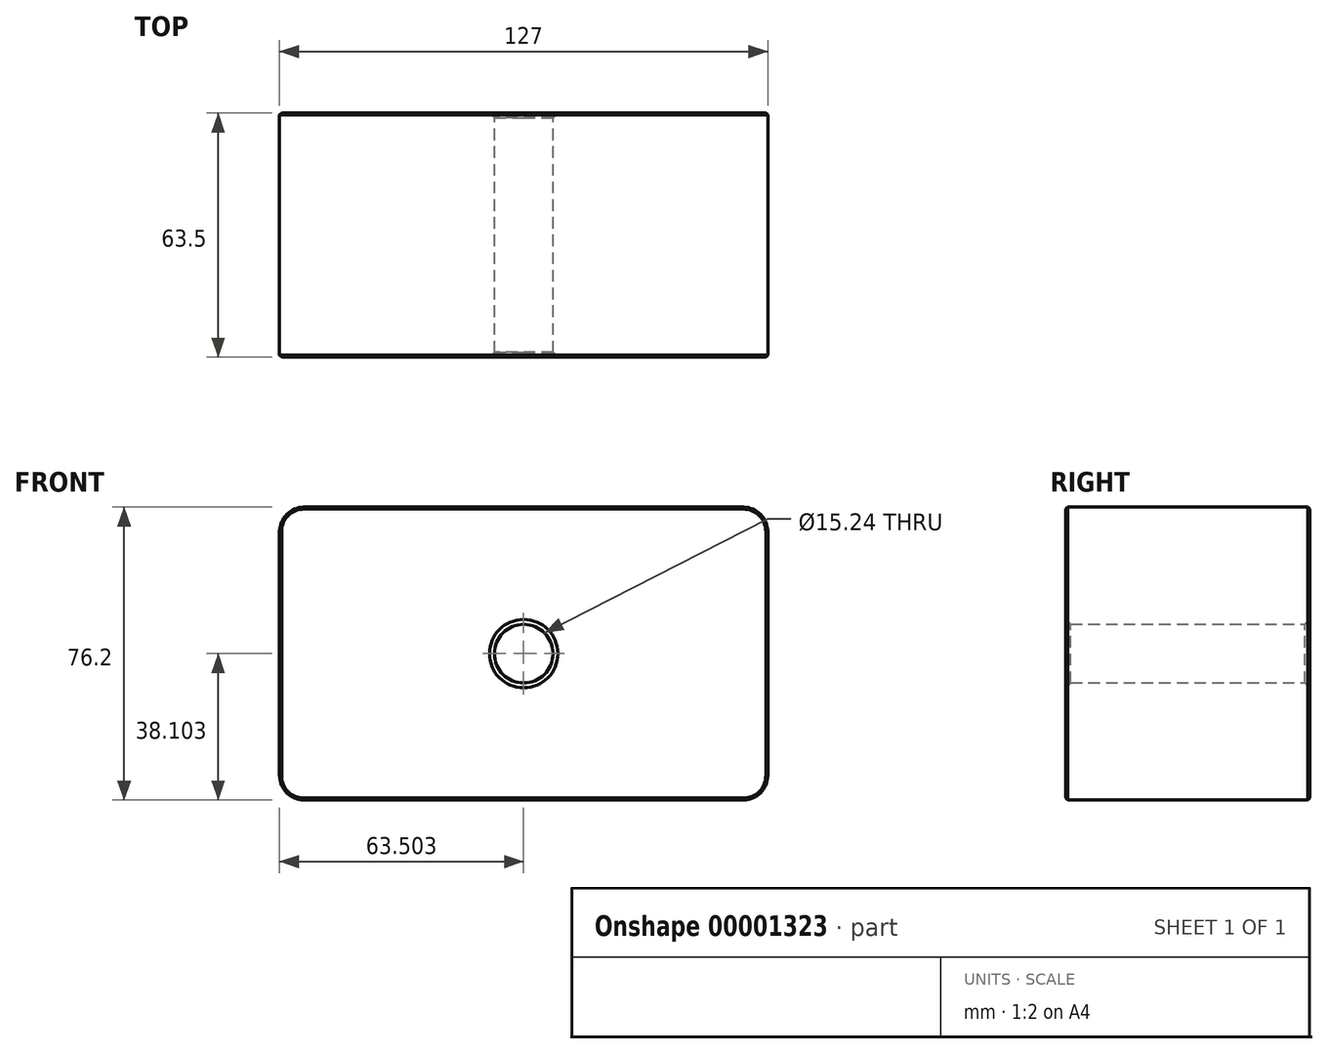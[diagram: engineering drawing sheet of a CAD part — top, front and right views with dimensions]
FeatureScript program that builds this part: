
annotation { "Feature Type Name" : "Feature", "Feature Type Description" : "" }
export const myFeature = defineFeature(function(context is Context, id is Id, definition is map)
    precondition{}
    {
        {
            var Q0;
            Q0=qCreatedBy(makeId("Front.planeOp"),FACE);
            var sketch = newSketch(context, id + "F0", { "sketchPlane" : qUnion([Q0])});
            skLineSegment(sketch, "E0.bottom", {"start": v(-20, 51.34) * mm, "end": v(94.3, 51.34) * mm});
            skLineSegment(sketch, "E0.top", {"start": v(-20, -24.86) * mm, "end": v(94.3, -24.86) * mm});
            skLineSegment(sketch, "E0.left", {"start": v(-26.36, 45) * mm, "end": v(-26.36, -18.5) * mm});
            skLineSegment(sketch, "E0.right", {"start": v(100.64, 45) * mm, "end": v(100.64, -18.5) * mm});
            skCircle(sketch, "E1", {"center": v(37.14, 13.24) * mm, "radius": 7.62 * mm});
            skPoint(sketch, "E2.visualSharp", {"position": v(-26.36, 51.34) * mm});
            skArc(sketch, "E2.filletArc", {"start": v(-20, 51.34) * mm, "mid": v(-24.5, 49.48) * mm, "end": v(-26.36, 45) * mm});
            skPoint(sketch, "E3.visualSharp", {"position": v(100.64, 51.34) * mm});
            skArc(sketch, "E3.filletArc", {"start": v(100.64, 45) * mm, "mid": v(98.78, 49.48) * mm, "end": v(94.3, 51.34) * mm});
            skPoint(sketch, "E4.visualSharp", {"position": v(100.64, -24.86) * mm});
            skArc(sketch, "E4.filletArc", {"start": v(94.3, -24.86) * mm, "mid": v(98.78, -23) * mm, "end": v(100.64, -18.5) * mm});
            skPoint(sketch, "E5.visualSharp", {"position": v(-26.36, -24.86) * mm});
            skArc(sketch, "E5.filletArc", {"start": v(-26.36, -18.5) * mm, "mid": v(-24.5, -23) * mm, "end": v(-20, -24.86) * mm});
            skSolve(sketch);
        }
        {
            var Q0;
            Q0=makeQuery(id+"F0.imprint","IMPRINT",FACE,{"disambiguationData":[TD([[makeQuery(id+"F0.imprint","IMPRINT",EDGE,{"derivedFrom":sQuery(id+"F0.wireOp",EDGE,"E0.bottom")}),-1.0]])]});
            extrude(context, id + "F1", {"entities" : qUnion([Q0]), "depth" : 63.5 * mm});
        }
        {
            var Q0;
            Q0=makeQuery(id+"F1.opExtrude","CAP_EDGE",EDGE,{"disambiguationData":[OSD([sQuery(id+"F0.wireOp",EDGE,"E1")])],"isStart":false});
            chamfer(context, id + "F2", {"entities" : qUnion([Q0]), "width" : 1.27 * mm, "tangentPropagation" : true});
        }
        {
            var Q0;
            Q0=makeQuery(id+"F1.opExtrude","CAP_EDGE",EDGE,{"disambiguationData":[OSD([sQuery(id+"F0.wireOp",EDGE,"E1")])],"isStart":true});
            chamfer(context, id + "F3", {"entities" : qUnion([Q0]), "width" : 1.27 * mm, "tangentPropagation" : true});
        }
        {
            var Q0;
            Q0=makeQuery(id+"F1.opExtrude","CAP_EDGE",EDGE,{"disambiguationData":[OSD([sQuery(id+"F0.wireOp",EDGE,"E0.right")])],"isStart":false});
            var Q1;
            Q1=makeQuery(id+"F1.opExtrude","CAP_EDGE",EDGE,{"disambiguationData":[OSD([sQuery(id+"F0.wireOp",EDGE,"E0.top")])],"isStart":false});
            var Q2;
            Q2=makeQuery(id+"F1.opExtrude","CAP_EDGE",EDGE,{"disambiguationData":[OSD([sQuery(id+"F0.wireOp",EDGE,"E4.filletArc")])],"isStart":false});
            var Q3;
            Q3=makeQuery(id+"F1.opExtrude","CAP_EDGE",EDGE,{"disambiguationData":[OSD([sQuery(id+"F0.wireOp",EDGE,"E0.bottom")])],"isStart":false});
            var Q4;
            Q4=makeQuery(id+"F1.opExtrude","CAP_EDGE",EDGE,{"disambiguationData":[OSD([sQuery(id+"F0.wireOp",EDGE,"E0.left")])],"isStart":false});
            var Q5;
            Q5=makeQuery(id+"F1.opExtrude","CAP_EDGE",EDGE,{"disambiguationData":[OSD([sQuery(id+"F0.wireOp",EDGE,"E2.filletArc")])],"isStart":false});
            var Q6;
            Q6=makeQuery(id+"F1.opExtrude","CAP_EDGE",EDGE,{"disambiguationData":[OSD([sQuery(id+"F0.wireOp",EDGE,"E5.filletArc")])],"isStart":false});
            var Q7;
            Q7=makeQuery(id+"F1.opExtrude","CAP_EDGE",EDGE,{"disambiguationData":[OSD([sQuery(id+"F0.wireOp",EDGE,"E3.filletArc")])],"isStart":false});
            chamfer(context, id + "F4", {"entities" : qUnion([Q0, Q1, Q2, Q3, Q4, Q5, Q6, Q7]), "width" : 0.5 * mm, "tangentPropagation" : true});
        }
        {
            var Q0;
            Q0=makeQuery(id+"F1.opExtrude","CAP_EDGE",EDGE,{"disambiguationData":[OSD([sQuery(id+"F0.wireOp",EDGE,"E0.top")])],"isStart":true});
            var Q1;
            Q1=makeQuery(id+"F1.opExtrude","CAP_EDGE",EDGE,{"disambiguationData":[OSD([sQuery(id+"F0.wireOp",EDGE,"E5.filletArc")])],"isStart":true});
            var Q2;
            Q2=makeQuery(id+"F1.opExtrude","CAP_EDGE",EDGE,{"disambiguationData":[OSD([sQuery(id+"F0.wireOp",EDGE,"E0.left")])],"isStart":true});
            var Q3;
            Q3=makeQuery(id+"F1.opExtrude","CAP_EDGE",EDGE,{"disambiguationData":[OSD([sQuery(id+"F0.wireOp",EDGE,"E0.bottom")])],"isStart":true});
            var Q4;
            Q4=makeQuery(id+"F1.opExtrude","CAP_EDGE",EDGE,{"disambiguationData":[OSD([sQuery(id+"F0.wireOp",EDGE,"E2.filletArc")])],"isStart":true});
            var Q5;
            Q5=makeQuery(id+"F1.opExtrude","CAP_EDGE",EDGE,{"disambiguationData":[OSD([sQuery(id+"F0.wireOp",EDGE,"E3.filletArc")])],"isStart":true});
            var Q6;
            Q6=makeQuery(id+"F1.opExtrude","CAP_EDGE",EDGE,{"disambiguationData":[OSD([sQuery(id+"F0.wireOp",EDGE,"E0.right")])],"isStart":true});
            var Q7;
            Q7=makeQuery(id+"F1.opExtrude","CAP_EDGE",EDGE,{"disambiguationData":[OSD([sQuery(id+"F0.wireOp",EDGE,"E4.filletArc")])],"isStart":true});
            chamfer(context, id + "F5", {"entities" : qUnion([Q0, Q1, Q2, Q3, Q4, Q5, Q6, Q7]), "width" : 0.5 * mm, "tangentPropagation" : true});
        }
    });
